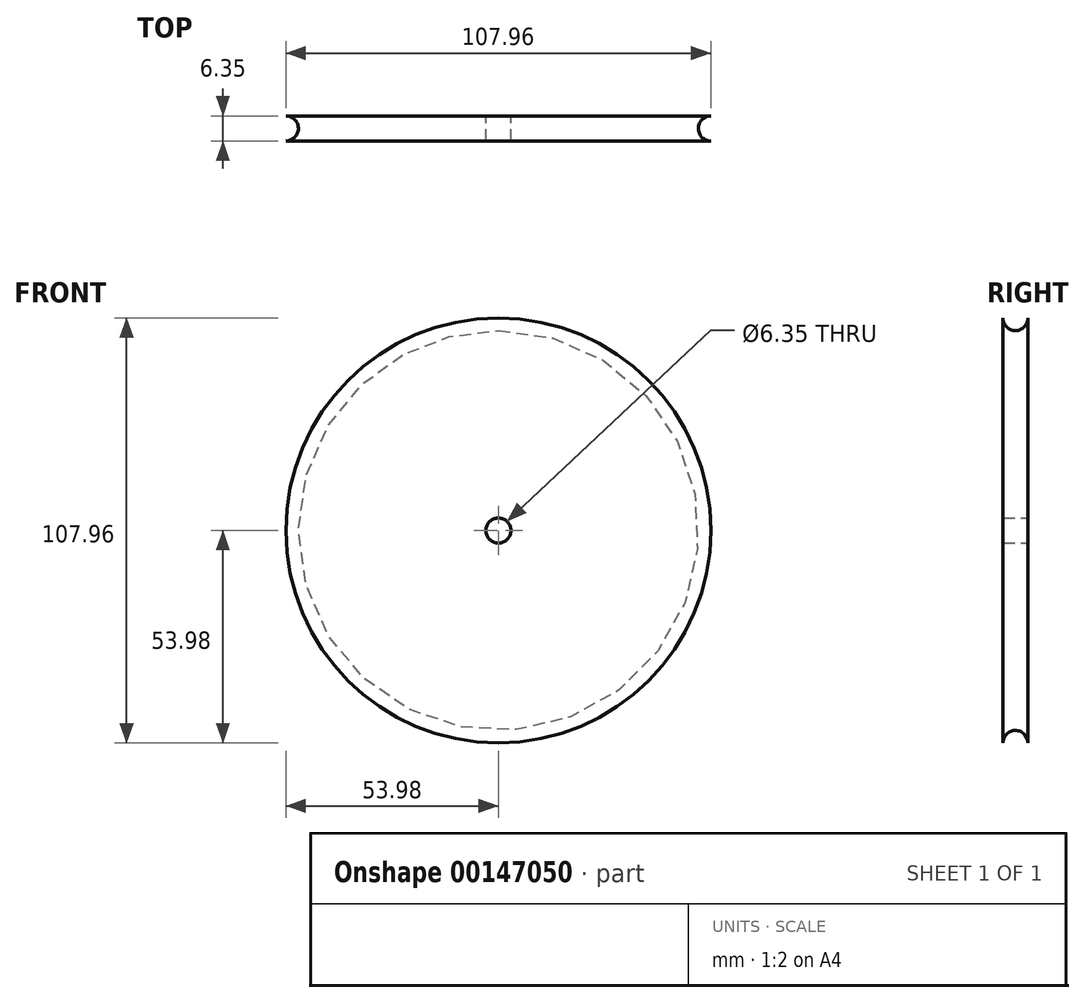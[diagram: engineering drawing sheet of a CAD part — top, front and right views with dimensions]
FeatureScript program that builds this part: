
annotation { "Feature Type Name" : "Feature", "Feature Type Description" : "" }
export const myFeature = defineFeature(function(context is Context, id is Id, definition is map)
    precondition{}
    {
        {
            var Q0;
            Q0=qCreatedBy(makeId("Top.planeOp"),FACE);
            var sketch = newSketch(context, id + "F0", { "sketchPlane" : qUnion([Q0])});
            skLineSegment(sketch, "E0.bottom", {"start": v(3.17, 5.39) * mm, "end": v(53.98, 5.39) * mm});
            skLineSegment(sketch, "E0.top", {"start": v(3.18, -0.96) * mm, "end": v(53.98, -0.96) * mm});
            skLineSegment(sketch, "E0.left", {"start": v(3.18, 5.39) * mm, "end": v(3.18, -0.96) * mm});
            skArc(sketch, "E1", {"start": v(53.98, 5.39) * mm, "mid": v(50.8, 2.21) * mm, "end": v(53.98, -0.96) * mm});
            skLineSegment(sketch, "E2", {"start": v(0, 49.76) * mm, "end": v(0, -43.86) * mm});
            skSolve(sketch);
        }
        {
            var Q0;
            Q0 = qSketchRegion(id + "F0", true);
            var Q1;
            Q1=sQuery(id+"F0.wireOp",EDGE,"E2");
            revolve(context, id + "F1", {"entities" : qUnion([Q0]), "axis" : qUnion([Q1]), "revolveType" : RevolveType.FULL});
        }
    });
